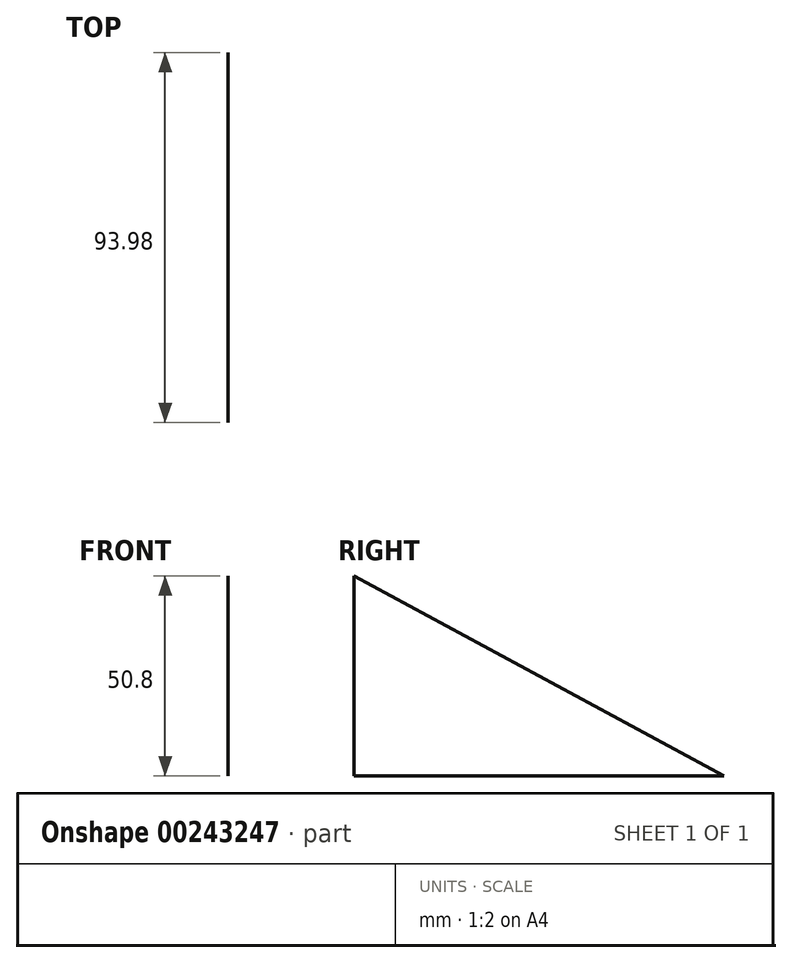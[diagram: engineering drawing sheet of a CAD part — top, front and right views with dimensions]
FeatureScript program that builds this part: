
annotation { "Feature Type Name" : "Feature", "Feature Type Description" : "" }
export const myFeature = defineFeature(function(context is Context, id is Id, definition is map)
    precondition{}
    {
        {
            var Q0;
            Q0=qCreatedBy(makeId("Right.planeOp"),FACE);
            var sketch = newSketch(context, id + "F0", { "sketchPlane" : qUnion([Q0])});
            skLineSegment(sketch, "E0", {"start": v(-53.11, 0) * mm, "end": v(40.87, 0) * mm});
            skLineSegment(sketch, "E1", {"start": v(40.87, 0) * mm, "end": v(-53.11, 50.8) * mm});
            skLineSegment(sketch, "E2", {"start": v(-53.11, 50.8) * mm, "end": v(-53.11, 0) * mm});
            skSolve(sketch);
        }
        {
            var Q0;
            Q0=makeQuery(id+"F0.imprint","IMPRINT",FACE,{"disambiguationData":[TD([[makeQuery(id+"F0.imprint","IMPRINT",EDGE,{"derivedFrom":sQuery(id+"F0.wireOp",EDGE,"E0")}),1.0]])]});
            extrude(context, id + "F1", {"entities" : qUnion([Q0]), "depth" : 1 / 203.2 * mm});
        }
    });
